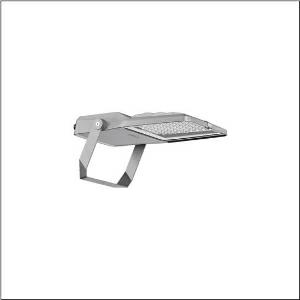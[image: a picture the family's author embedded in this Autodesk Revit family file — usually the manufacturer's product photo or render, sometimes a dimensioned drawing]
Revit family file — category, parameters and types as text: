
# Revit family: floodlight_fl_21_iq_mini___pl64_5xa7771b4e1a_e45f
name_source: partatom
category: Lighting Fixtures
units: mm (PartAtom-declared; Revit-internal decimal feet)

## family parameters
Cut with Voids When Loaded = No
Host = Face
Light Source = No
Part Type = Normal
Room Calculation Point = No
Round Connector Dimension = Use Diameter
Shared = No

## types (1)
- --- (1 x LED, 6270 lm, 45.5 W, 4000K)
    Apparent Load = 46 VA
    CIE Flux Codes = 28 80 98 100 100
    Color Rendering = 70
    Color Temperature = 4000K
    Default Elevation = 1800 mm
    Description = Floodlight FL 21 iQ mini, floodlight, primary light control with lens, of PMMA, primary optical cover: protective disc, of toughened safety glass, transparent, light distribution: PL64, light emission: direct distribution, installation type: surface-mounted, LED, High Power LED, rated luminous flux: 6.270lm, luminous efficacy: 138lm/W, light colour: 740, colour temperature: 4000K, control gear: iQ Comfort/DALI, control: Auto-Match, Temp-Guard, Lumen-Switch, Night-Set, Smart-Wire, Light-Fading, Desk-Remote (wireless, voltage-free reading and setting of iQ features in the workshop via application-optimized NFC function/RFID function), optimised constant luminous flux control (CLO 2.0), with terminal, 6-pole, mains connection: 220..240V, AC, 50/60Hz, start of lifetime: 46W, end of service life: 48W, reduction: 22W, luminaire housing, of diecast aluminium, powder-coated, Siteco® metallic grey (DB 702S), corrosivity category C5 mid according to DIN EN ISO 12944, suitable for swimming pools, chlorine-resistant, sealing non-destructively replaceable, mounting bracket, of steel, galvanised, powder-coated, Siteco® metallic grey (DB 702S), protection rating (complete): IP66, insulation class (complete): insulation class II (safety insulation), certification: CE, ENEC, VDE, protection symbol: D, impact resistance: IK08, permissible operating ambient temperature: -40..+40°C, permissible operating ambient temperature for outdoor applications: -40..+50°C, standard: DIN EN 12944, LABS conformity tested according to VDMA 24364:2018-05, packaging unit: 1 piece

Light Distribution: PL64
    Height = 70 mm
    Lamp = 1 x LED
    Lamp Light Flux = 6270 lm
    Lamp Power = 45.5 W
    Lamp count = 1
    Length = 485 mm
    Luminous efficacy = 138 lm/W
    Manufacturer = Siteco
    ModVariant = No
    Model = 5XA7771B4E1A
    Mounting Place = Wall
    Mounting Type = Surface mounted
    Number of Poles = 1
    OnlyDefault = Yes
    Power Factor = 1
    Product Name = Floodlight FL 21 iQ mini | PL64
    Product group = floodlight | wall mounted
    ProductGroupID = 2001
    Protection Class = Protection class II
    Protection Degree = IP 66
    RLX_Detail_Level = 1
    RLX_Emergency_Light_Flux = 0 lm
    RLX_Emergency_Type = 0
    RLX_Emergency_Type_DB = No
    RlxData = <blob elided: 96345 chars, md5=a31258fe>
    Socket = socket
    Standby Power = 0 W
    System Light Flux = 6270 lm
    System Power = 46 W
    Type Comments = factory setting: luminous flux: 100 % | dim-lin: 254 | 463 mA
    Type Image = l_1006845.jpg
    URL = http://relux.com
    VarID = @adj_167118
    Voltage = 0 V
    Weight = 0.00 kg
    Width = 337 mm

## geometry (parser evidence)
native form markers: Blend x4, Sweep x13
no freeform markers — native parametric forms only
